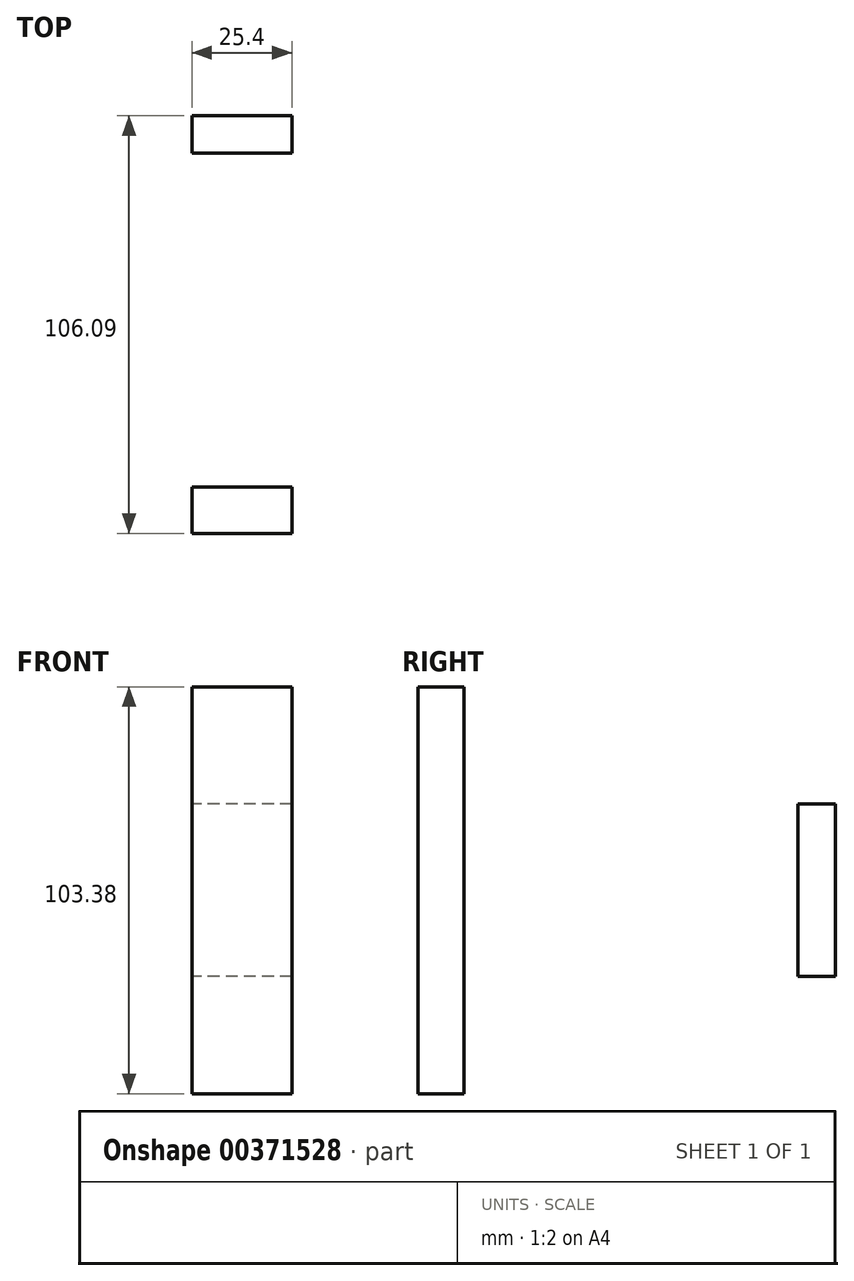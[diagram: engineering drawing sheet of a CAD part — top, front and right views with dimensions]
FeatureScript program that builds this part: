
annotation { "Feature Type Name" : "Feature", "Feature Type Description" : "" }
export const myFeature = defineFeature(function(context is Context, id is Id, definition is map)
    precondition{}
    {
        {
            var Q0;
            Q0=qCreatedBy(makeId("Right.planeOp"),FACE);
            var sketch = newSketch(context, id + "F0", { "sketchPlane" : qUnion([Q0])});
            skLineSegment(sketch, "E0.bottom", {"start": v(-48.94, 51.69) * mm, "end": v(-60.71, 51.69) * mm});
            skLineSegment(sketch, "E0.top", {"start": v(-48.94, -51.69) * mm, "end": v(-60.71, -51.69) * mm});
            skLineSegment(sketch, "E0.left", {"start": v(-48.94, 51.69) * mm, "end": v(-48.94, -51.69) * mm});
            skLineSegment(sketch, "E0.right", {"start": v(-60.71, 51.69) * mm, "end": v(-60.71, -51.69) * mm});
            skPoint(sketch, "E0.middle", {"position": v(-54.82, 0) * mm});
            skLineSegment(sketch, "E1.bottom", {"start": v(35.85, 21.9) * mm, "end": v(45.38, 21.9) * mm});
            skLineSegment(sketch, "E1.top", {"start": v(35.85, -21.9) * mm, "end": v(45.38, -21.9) * mm});
            skLineSegment(sketch, "E1.left", {"start": v(35.85, 21.9) * mm, "end": v(35.85, -21.9) * mm});
            skLineSegment(sketch, "E1.right", {"start": v(45.38, 21.9) * mm, "end": v(45.38, -21.9) * mm});
            skPoint(sketch, "E1.middle", {"position": v(40.62, 0) * mm});
            skSolve(sketch);
        }
        {
            var Q0;
            Q0=makeQuery(id+"F0.imprint","IMPRINT",FACE,{"disambiguationData":[TD([[makeQuery(id+"F0.imprint","IMPRINT",EDGE,{"derivedFrom":sQuery(id+"F0.wireOp",EDGE,"E0.bottom")}),1.0]])]});
            var Q1;
            Q1=makeQuery(id+"F0.imprint","IMPRINT",FACE,{"disambiguationData":[TD([[makeQuery(id+"F0.imprint","IMPRINT",EDGE,{"derivedFrom":sQuery(id+"F0.wireOp",EDGE,"E1.bottom")}),-1.0]])]});
            extrude(context, id + "F1", {"entities" : qUnion([Q0, Q1]), "depth" : 25.4 * mm});
        }
    });
